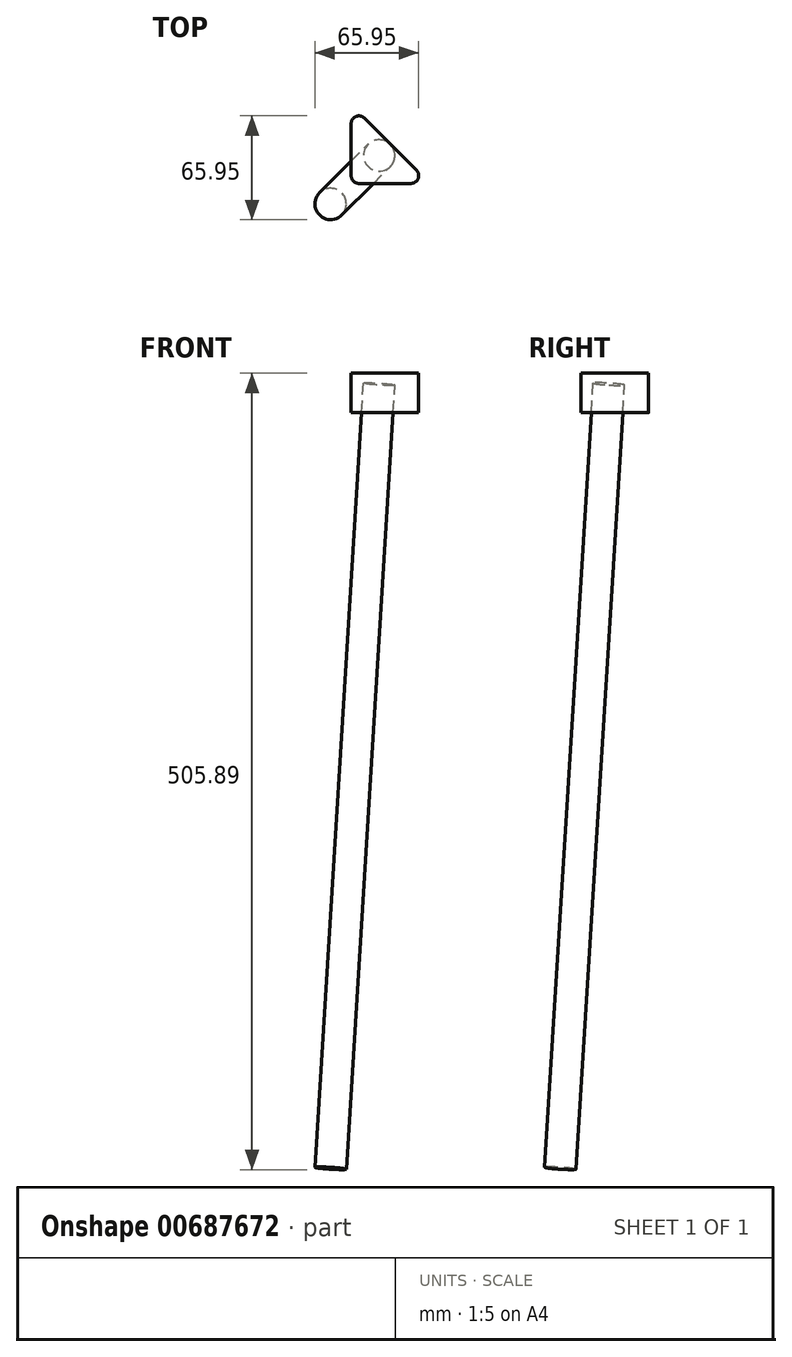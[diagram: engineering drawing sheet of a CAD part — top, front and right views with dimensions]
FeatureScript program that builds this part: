
annotation { "Feature Type Name" : "Feature", "Feature Type Description" : "" }
export const myFeature = defineFeature(function(context is Context, id is Id, definition is map)
    precondition{}
    {
        {
            var Q0;
            Q0=qCreatedBy(makeId("Top.planeOp"),FACE);
            var sketch = newSketch(context, id + "F0", { "sketchPlane" : qUnion([Q0])});
            skLineSegment(sketch, "E0", {"start": v(0, 5) * mm, "end": v(0, 37.93) * mm});
            skLineSegment(sketch, "E1", {"start": v(8.54, 41.46) * mm, "end": v(41.46, 8.54) * mm});
            skLineSegment(sketch, "E2", {"start": v(37.93, 0) * mm, "end": v(5, 0) * mm});
            skPoint(sketch, "E3.visualSharp", {"position": v(0, 50) * mm});
            skArc(sketch, "E3.filletArc", {"start": v(8.54, 41.46) * mm, "mid": v(3.09, 42.55) * mm, "end": v(0, 37.93) * mm});
            skPoint(sketch, "E4.visualSharp", {"position": v(50, 0) * mm});
            skArc(sketch, "E4.filletArc", {"start": v(37.93, 0) * mm, "mid": v(42.55, 3.09) * mm, "end": v(41.46, 8.54) * mm});
            skPoint(sketch, "E5.visualSharp", {"position": v(0, 0) * mm});
            skArc(sketch, "E5.filletArc", {"start": v(0, 5) * mm, "mid": v(1.46, 1.46) * mm, "end": v(5, 0) * mm});
            skLineSegment(sketch, "E6", {"start": v(5, 5) * mm, "end": v(25, 25) * mm, "construction": true});
            skSolve(sketch);
        }
        {
            var Q0;
            Q0=qCreatedBy(makeId("Top.planeOp"),FACE);
            var sketch = newSketch(context, id + "F1", { "sketchPlane" : qUnion([Q0])});
            skCircle(sketch, "E7", {"center": v(0, 0) * mm, "radius": 10 * mm});
            skSolve(sketch);
        }
        {
            var Q0;
            Q0 = qSketchRegion(id + "F1", true);
            extrude(context, id + "F2", {"entities" : qUnion([Q0]), "oppositeDirection" : true, "depth" : 500 * mm, "offsetDistance" : 25 * mm});
        }
        {
            var Q0;
            Q0=makeQuery(id+"F2.opExtrude","SWEPT_BODY",BODY,{"disambiguationData":[OSD([sQuery(id+"F1.wireOp",EDGE,"E7")])]});
            var Q1;
            Q1=sQuery(id+"F0.wireOp",EDGE,"E1");
            transform(context, id + "F3", {"entities" : qUnion([Q0]), "transformType" : TransformType.ROTATION, "transformAxis" : qUnion([Q1]), "angle" : 5 * degree, "oppositeDirection" : true, "makeCopy" : false});
        }
        {
            var Q0;
            Q0=makeQuery(id+"F2.opExtrude","SWEPT_BODY",BODY,{"disambiguationData":[OSD([sQuery(id+"F1.wireOp",EDGE,"E7")])]});
            var Q1;
            Q1=sQuery(id+"F0.wireOp",EDGE,"E6");
            transform(context, id + "F4", {"entities" : qUnion([Q0]), "transformType" : TransformType.TRANSLATION_DISTANCE, "transformDirection" : qUnion([Q1]), "distance" : 25 * mm, "makeCopy" : false});
        }
        {
            var Q0;
            Q0=makeQuery(id+"F2.opExtrude","SWEPT_BODY",BODY,{"disambiguationData":[OSD([sQuery(id+"F1.wireOp",EDGE,"E7")])]});
            var Q1;
            Q1=qCreatedBy(makeId("Top.planeOp"),FACE);
            transform(context, id + "F5", {"entities" : qUnion([Q0]), "transformType" : TransformType.TRANSLATION_DISTANCE, "transformDirection" : qUnion([Q1]), "distance" : 10 * mm, "oppositeDirection" : true, "makeCopy" : false});
        }
        {
            var Q0;
            Q0=makeQuery(id+"F0.imprint","IMPRINT",FACE,{"disambiguationData":[TD([[makeQuery(id+"F0.imprint","IMPRINT",EDGE,{"derivedFrom":sQuery(id+"F0.wireOp",EDGE,"E0")}),-1.0]])]});
            extrude(context, id + "F6", {"entities" : qUnion([Q0]), "oppositeDirection" : true, "depth" : 25 * mm, "offsetDistance" : 25 * mm});
        }
    });
